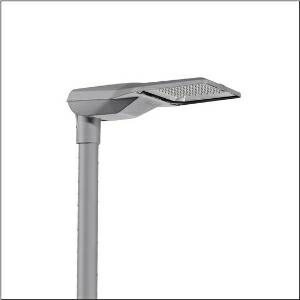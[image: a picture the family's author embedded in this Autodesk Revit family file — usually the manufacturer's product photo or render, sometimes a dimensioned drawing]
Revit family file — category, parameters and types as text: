
# Revit family: streetlight_sl_21_midi___stw1_0a_5xe7e43a08mb_7906
name_source: partatom
category: Lighting Fixtures
units: mm (PartAtom-declared; Revit-internal decimal feet)

## family parameters
Cut with Voids When Loaded = No
Host = Face
Light Source = No
Part Type = Normal
Room Calculation Point = No
Round Connector Dimension = Use Diameter
Shared = No

## types (1)
- --- (1 x LED, 20180 lm, 147 W, 4000K)
    Apparent Load = 147 VA
    CIE Flux Codes = 38 75 98 100 100
    Color Rendering = 70
    Color Temperature = 4000K
    Default Elevation = 1800 mm
    Description = Streetlight SL 21 midi, mast luminaire, primary light control with lens, of PMMA, primary optical cover: cover, of toughened safety glass, transparent, light distribution: STW1.0a, light emission: direct distribution, primary light characteristic: asymmetric, installation type: post-top, side-entry, LED, 3G 1.5mm², High Power LED, rated luminous flux: 20.180lm, luminous efficacy: 137lm/W, light colour: 740, colour temperature: 4000K, control gear: Easy, control: overheat protection, constant luminous flux control, time-dependent luminous flux control, flexible luminous flux parameterisation, mains connection: 220..240V, AC, 50/60Hz, connection cable pre-assembled, cable length: 12,5m, wiring characteristics: H07RN-F, start of lifetime: 147W, end of service life: 155W, reduction: 64W, luminaire housing, of diecast aluminium, powder-coated, Siteco® metallic grey (DB 702S), corrosivity category C5 mid according to DIN EN ISO 12944, please order mast flange separately, inclination adjustable: 0°, 5°, 10°, 15°, sealing non-destructively replaceable, multi-level sealing system, length: 644mm, width: 335mm, height: 110mm, mast flange for spigot size: 42mm (side-entry): 5XC10008XM4, 60/48mm (side-entry/post-top): 5XC10108XM2, 76/60mm (side-entry/post-top): 5XC10108XM1, mounting height: 4..8m, protection rating (complete): IP66, insulation class (complete): insulation class II (safety insulation), certification: CE, ENEC, ENEC+, VDE, impact resistance: IK10, permissible operating ambient temperature for outdoor applications: -40..+50°C, standard-compliant lighting for roads and squares, packaging unit: 1 piece

Light Distribution: STW1.0a
    Height = 111 mm
    Lamp = 1 x LED
    Lamp Light Flux = 20180 lm
    Lamp Power = 147 W
    Lamp count = 1
    Length = 644 mm
    Luminous efficacy = 137 lm/W
    Manufacturer = Siteco
    ModVariant = No
    Model = 5XE7E43A08MB
    Number of Poles = 1
    OnlyDefault = Yes
    Power Factor = 1
    Product Name = Streetlight SL 21 midi | STW1.0a
    Product group = mast luminaire | pylon top
    ProductGroupID = 6100
    Protection Class = Protection class II
    Protection Degree = IP 66
    RLX_Detail_Level = 1
    RLX_Emergency_Light_Flux = 0 lm
    RLX_Emergency_Type = 0
    RLX_Emergency_Type_DB = No
    RlxData = <blob elided: 26821 chars, md5=0e3209de>
    Socket = socket
    Standby Power = 0 W
    System Light Flux = 20180 lm
    System Power = 147 W
    Type Comments = factory setting: luminous flux: 100 % | Output Level: 100 % | 750 mA
    Type Image = l_1004298.jpg
    URL = http://relux.com
    VarID = @adj_208935
    Voltage = 0 V
    Weight = 0.00 kg
    Width = 336 mm

## geometry (parser evidence)
native form markers: Blend x4, Sweep x9
no freeform markers — native parametric forms only
